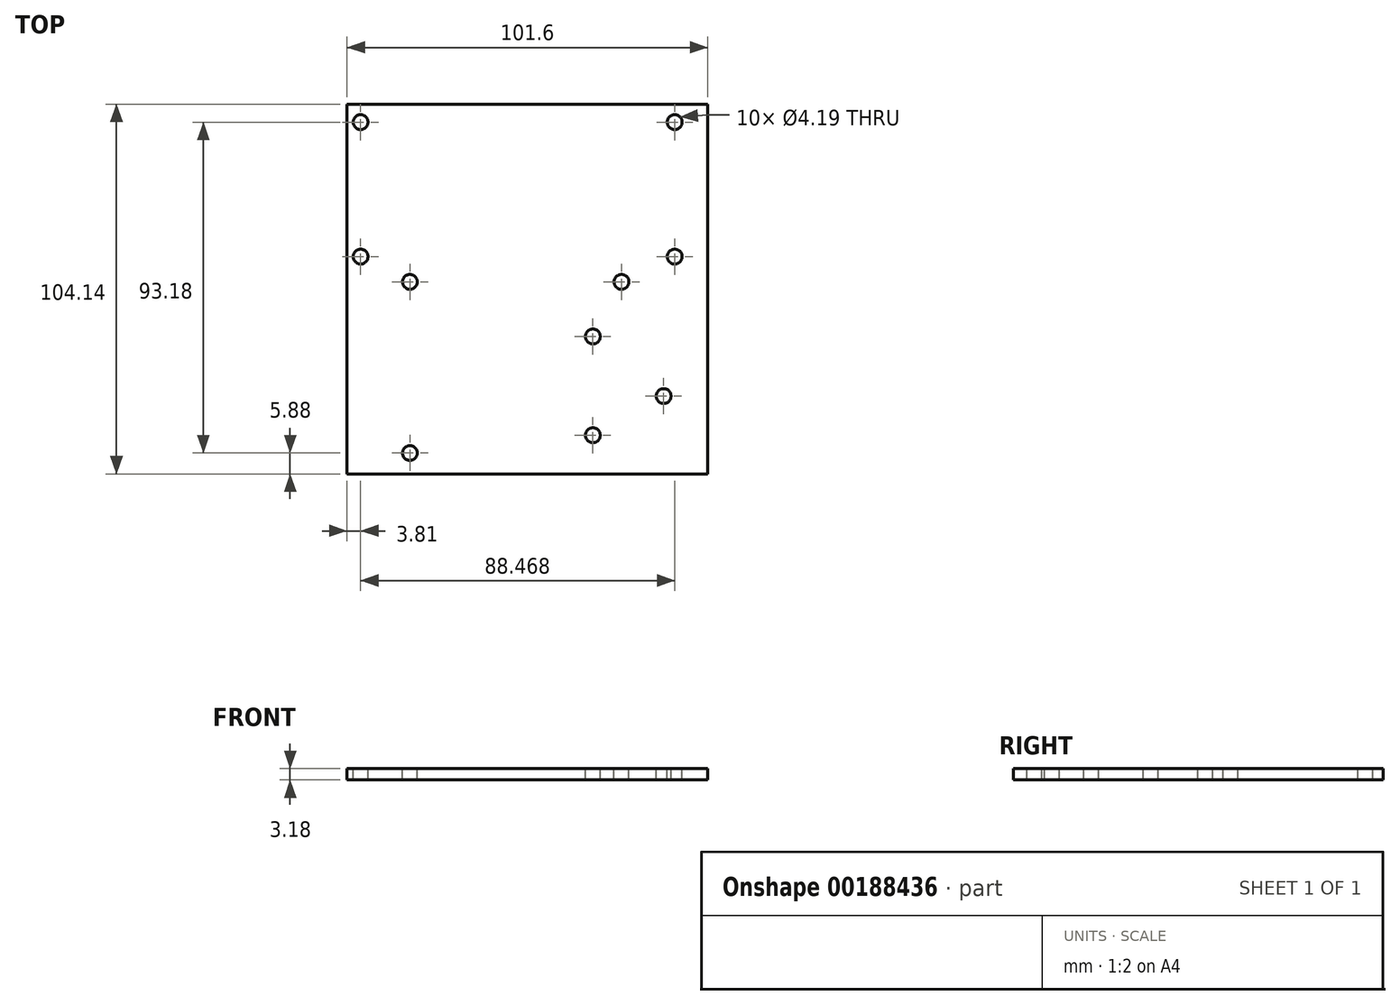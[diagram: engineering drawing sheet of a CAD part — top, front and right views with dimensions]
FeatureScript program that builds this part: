
annotation { "Feature Type Name" : "Feature", "Feature Type Description" : "" }
export const myFeature = defineFeature(function(context is Context, id is Id, definition is map)
    precondition{}
    {
        {
            var Q0;
            Q0=qCreatedBy(makeId("Top.planeOp"),FACE);
            var sketch = newSketch(context, id + "F0", { "sketchPlane" : qUnion([Q0])});
            skLineSegment(sketch, "E0.bottom", {"start": v(0, 0) * mm, "end": v(101.6, 0) * mm});
            skLineSegment(sketch, "E0.top", {"start": v(0, -104.14) * mm, "end": v(101.6, -104.14) * mm});
            skLineSegment(sketch, "E0.left", {"start": v(0, 0) * mm, "end": v(0, -104.14) * mm});
            skLineSegment(sketch, "E0.right", {"start": v(101.6, 0) * mm, "end": v(101.6, -104.14) * mm});
            skLineSegment(sketch, "E1.0", {"start": v(3.8, 0) * mm, "end": v(3.81, -104.14) * mm});
            skLineSegment(sketch, "E2.0", {"start": v(0, -5.08) * mm, "end": v(101.6, -5.08) * mm});
            skPoint(sketch, "E3", {"position": v(3.81, -5.08) * mm});
            skPoint(sketch, "E4", {"position": v(3.81, -42.95) * mm});
            skPoint(sketch, "E5", {"position": v(92.28, -5.08) * mm});
            skPoint(sketch, "E6", {"position": v(92.28, -42.95) * mm});
            skLineSegment(sketch, "E7", {"start": v(3.81, -42.95) * mm, "end": v(92.28, -42.95) * mm});
            skLineSegment(sketch, "E8.0", {"start": v(3.81, -50.06) * mm, "end": v(92.28, -50.06) * mm});
            skPoint(sketch, "E9", {"position": v(3.81, -50.06) * mm});
            skPoint(sketch, "E10", {"position": v(17.7, -50.06) * mm});
            skPoint(sketch, "E11", {"position": v(17.7, -98.26) * mm});
            skPoint(sketch, "E12", {"position": v(69.22, -93.26) * mm});
            skPoint(sketch, "E13", {"position": v(69.22, -65.44) * mm});
            skPoint(sketch, "E14", {"position": v(77.3, -50.06) * mm});
            skPoint(sketch, "E15", {"position": v(89.15, -82.22) * mm});
            skCircle(sketch, "E16", {"center": v(3.81, -5.08) * mm, "radius": 2.1 * mm});
            skCircle(sketch, "E17", {"center": v(92.28, -5.08) * mm, "radius": 2.1 * mm});
            skCircle(sketch, "E18", {"center": v(3.81, -42.95) * mm, "radius": 2.1 * mm});
            skCircle(sketch, "E19", {"center": v(92.28, -42.95) * mm, "radius": 2.1 * mm});
            skCircle(sketch, "E20", {"center": v(17.7, -50.06) * mm, "radius": 2.1 * mm});
            skCircle(sketch, "E21", {"center": v(17.7, -98.26) * mm, "radius": 2.1 * mm});
            skCircle(sketch, "E22", {"center": v(69.22, -65.44) * mm, "radius": 2.1 * mm});
            skCircle(sketch, "E23", {"center": v(69.22, -93.26) * mm, "radius": 2.1 * mm});
            skCircle(sketch, "E24", {"center": v(89.15, -82.22) * mm, "radius": 2.1 * mm});
            skCircle(sketch, "E25", {"center": v(77.3, -50.06) * mm, "radius": 2.1 * mm});
            skLineSegment(sketch, "E26.0", {"start": v(-3.18, 3.17) * mm, "end": v(104.78, 3.17) * mm});
            skLineSegment(sketch, "E26.1", {"start": v(-3.18, 3.17) * mm, "end": v(-3.17, -107.31) * mm});
            skLineSegment(sketch, "E26.2", {"start": v(-3.17, -107.31) * mm, "end": v(104.78, -107.31) * mm});
            skLineSegment(sketch, "E26.3", {"start": v(104.78, 3.17) * mm, "end": v(104.78, -107.31) * mm});
            skSolve(sketch);
        }
        {
            var Q0;
            {var subQ0=sQuery(id+"F0.wireOp",EDGE,"E1.0");var subQ1=makeQuery(id+"F0.imprint","IMPRINT",VERTEX,{"derivedFrom":subQ0});Q0=makeQuery(id+"F0.imprint","IMPRINT",FACE,{"disambiguationData":[TD([[makeQuery(id+"F0.imprint","IMPRINT",EDGE,{"disambiguationData":[TD([[subQ1,1.0]])],"derivedFrom":subQ0}),-1.0]])]});}
            var Q1;
            {var subQ1=sQuery(id+"F0.wireOp",EDGE,"E0.bottom");var subQ5=sQuery(id+"F0.wireOp",EDGE,"E0.left");var subQ6=makeQuery(id+"F0.imprint","INTERSECT",VERTEX,{"derivedFrom":[subQ1,subQ5]});Q1=makeQuery(id+"F0.imprint","IMPRINT",FACE,{"disambiguationData":[TD([[makeQuery(id+"F0.imprint","IMPRINT",EDGE,{"disambiguationData":[TD([[subQ6,-1.0]])],"derivedFrom":subQ1}),-1.0]])]});}
            var Q2;
            {var subQ1=sQuery(id+"F0.wireOp",EDGE,"E0.bottom");var subQ5=sQuery(id+"F0.wireOp",EDGE,"E0.right");var subQ6=makeQuery(id+"F0.imprint","INTERSECT",VERTEX,{"derivedFrom":[subQ1,subQ5]});Q2=makeQuery(id+"F0.imprint","IMPRINT",FACE,{"disambiguationData":[TD([[makeQuery(id+"F0.imprint","IMPRINT",EDGE,{"disambiguationData":[TD([[subQ6,1.0]])],"derivedFrom":subQ1}),-1.0]])]});}
            var Q3;
            Q3=makeQuery(id+"F0.imprint","IMPRINT",FACE,{"disambiguationData":[TD([[makeQuery(id+"F0.imprint","IMPRINT",EDGE,{"derivedFrom":sQuery(id+"F0.wireOp",EDGE,"E19")}),-1.0]])]});
            extrude(context, id + "F1", {"entities" : qUnion([Q0, Q1, Q2, Q3]), "oppositeDirection" : true, "depth" : 3.17 * mm});
        }
    });
